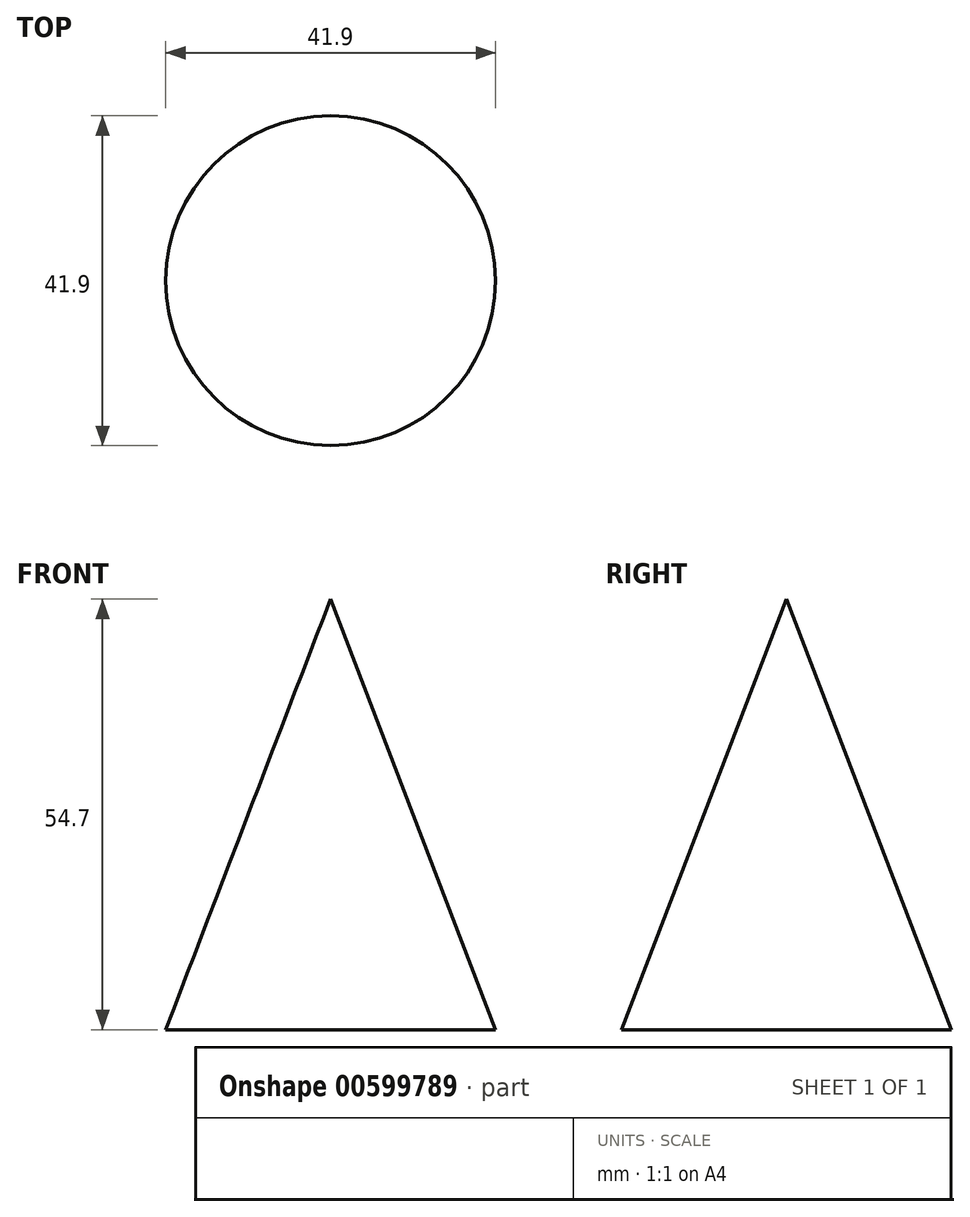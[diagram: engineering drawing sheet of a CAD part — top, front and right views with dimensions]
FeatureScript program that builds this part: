
annotation { "Feature Type Name" : "Feature", "Feature Type Description" : "" }
export const myFeature = defineFeature(function(context is Context, id is Id, definition is map)
    precondition{}
    {
        {
            var Q0;
            Q0=qCreatedBy(makeId("Front.planeOp"),FACE);
            var sketch = newSketch(context, id + "F0", { "sketchPlane" : qUnion([Q0])});
            skLineSegment(sketch, "E0", {"start": v(0, 54.7) * mm, "end": v(-20.95, 0) * mm});
            skLineSegment(sketch, "E1", {"start": v(-20.95, 0) * mm, "end": v(0, 0) * mm});
            skLineSegment(sketch, "E2", {"start": v(0, 0) * mm, "end": v(0, 54.7) * mm});
            skSolve(sketch);
        }
        {
            var Q0;
            Q0=makeQuery(id+"F0.imprint","IMPRINT",FACE,{"disambiguationData":[TD([[makeQuery(id+"F0.imprint","IMPRINT",EDGE,{"derivedFrom":sQuery(id+"F0.wireOp",EDGE,"E0")}),1.0]])]});
            var Q1;
            Q1=sQuery(id+"F0.wireOp",EDGE,"E2");
            revolve(context, id + "F1", {"entities" : qUnion([Q0]), "axis" : qUnion([Q1]), "revolveType" : RevolveType.FULL});
        }
    });
